# Revit family: Shower-Valve_Trim-KOHLER-Composed-K-TS73115
name_source: partatom
category: Plumbing Fixtures
revit_build: Autodesk Revit 2015 (Build: 20140606_1530(x64)
units: mm (PartAtom-declared; Revit-internal decimal feet)

## types (4) — shared parameters
ADA Compliant = Yes
Assembly Code = D2010700
CW Connection = No
Cold Water Inlet = Cold Water Inlet
Date Modified = 09/10/2018
Default Elevation = 42"
Drain Included = No
HW Connection = No
Height = 6 3/8"
Hot Water Inlet = Hot Water Inlet
Manufacturer = KOHLER Co.
MasterFormat 1995 = 15410
MasterFormat 2004 = 22.41.23
Material = Premium Metal Construction
Product Documentation Link = https://www.us.kohler.com
Product Name = Composed
Product Page URL = https://www.us.kohler.com
URL = https://www.us.kohler.com
Vent Connection = No
Waste Connection = No
Waste Water Outlet = Waste Water Outlet
Width = 6 3/8"

## per-type parameters (varying)
| type | Cross Lever Handle | Description | Finish | Lever Handle | Model | Type |
| Cross Lever Handle, CP-Polished Chrome | Yes | Rite-Temp valve trim with cross handle | Kohler-Metal-CP-Polished_Chrome | No | K-TS73115-3-CP | 1 |
| Cross Lever Handle, TT-Titanium | Yes | Rite-Temp valve trim with cross handle | Kohler-Metal-TT-Vibrant_Titanium | No | K-TS73115-3-TT | 2 |
| Lever Handle, CP-Polished Chrome | No | Rite-Temp valve trim with lever handle | Kohler-Metal-CP-Polished_Chrome | Yes | K-TS73115-4-CP | 3 |
| Lever Handle, TT-Titanium | No | Rite-Temp valve trim with lever handle | Kohler-Metal-TT-Vibrant_Titanium | Yes | K-TS73115-4-TT | 4 |

## geometry (parser evidence)
native form markers: Sweep x5
no freeform markers — native parametric forms only
